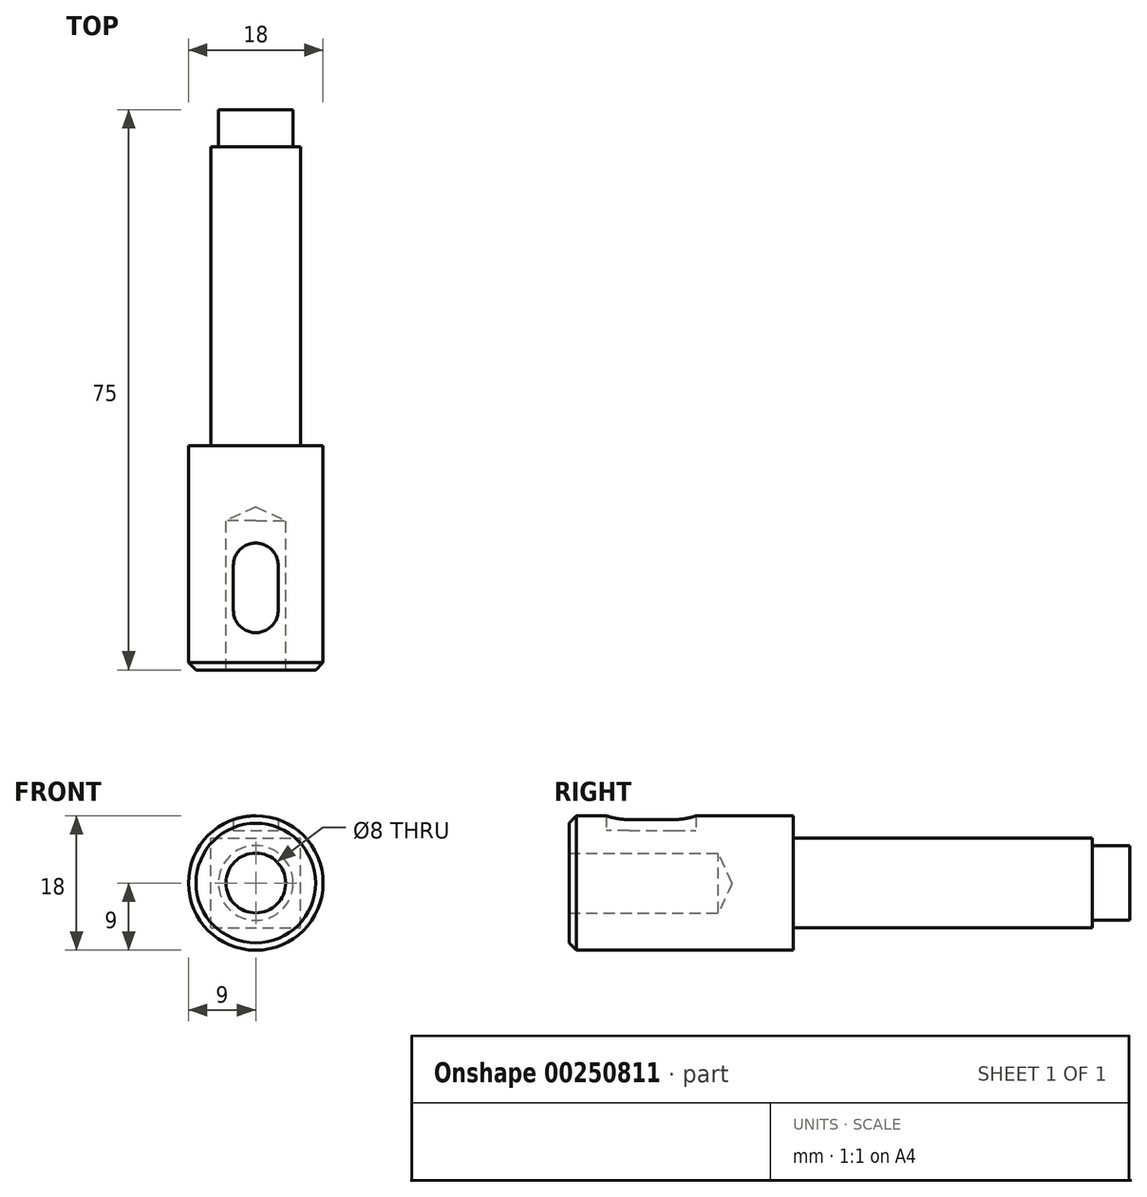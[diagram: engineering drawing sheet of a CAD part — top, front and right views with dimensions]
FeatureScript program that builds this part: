
annotation { "Feature Type Name" : "Feature", "Feature Type Description" : "" }
export const myFeature = defineFeature(function(context is Context, id is Id, definition is map)
    precondition{}
    {
        {
            var Q0;
            Q0=qCreatedBy(makeId("Top.planeOp"),FACE);
            var sketch = newSketch(context, id + "F0", { "sketchPlane" : qUnion([Q0])});
            skLineSegment(sketch, "E0", {"start": v(0, 53.17) * mm, "end": v(5, 53.17) * mm});
            skLineSegment(sketch, "E1", {"start": v(5, 53.17) * mm, "end": v(5, 48.17) * mm});
            skLineSegment(sketch, "E2", {"start": v(5, 48.17) * mm, "end": v(6, 48.17) * mm});
            skLineSegment(sketch, "E3", {"start": v(6, 48.17) * mm, "end": v(6, 8.17) * mm});
            skLineSegment(sketch, "E4", {"start": v(6, 8.17) * mm, "end": v(9, 8.17) * mm});
            skLineSegment(sketch, "E5", {"start": v(9, 8.17) * mm, "end": v(9, -20.83) * mm});
            skLineSegment(sketch, "E6", {"start": v(9, -20.83) * mm, "end": v(8, -21.83) * mm});
            skLineSegment(sketch, "E7", {"start": v(8, -21.83) * mm, "end": v(4, -21.83) * mm});
            skLineSegment(sketch, "E8", {"start": v(4, -21.83) * mm, "end": v(4, -6.83) * mm});
            skLineSegment(sketch, "E9", {"start": v(4, -6.83) * mm, "end": v(4, -1.83) * mm});
            skLineSegment(sketch, "E10", {"start": v(4, -1.83) * mm, "end": v(0, 0) * mm});
            skLineSegment(sketch, "E11", {"start": v(0, 53.17) * mm, "end": v(0, 0) * mm});
            skSolve(sketch);
        }
        {
            var Q0;
            Q0=makeQuery(id+"F0.imprint","IMPRINT",FACE,{"disambiguationData":[TD([[makeQuery(id+"F0.imprint","IMPRINT",EDGE,{"derivedFrom":sQuery(id+"F0.wireOp",EDGE,"E0")}),-1.0]])]});
            var Q1;
            Q1=sQuery(id+"F0.wireOp",EDGE,"E11");
            revolve(context, id + "F1", {"surfaceOperationType" : NewSurfaceOperationType.NEW, "entities" : qUnion([Q0]), "axis" : qUnion([Q1]), "revolveType" : RevolveType.FULL});
        }
        {
            var Q0;
            Q0=qCreatedBy(makeId("Top.planeOp"),FACE);
            cPlane(context, id + "F2", {"entities" : qUnion([Q0]), "cplaneType" : CPlaneType.OFFSET, "offset" : 7 * mm, "width" : 150 * mm, "height" : 150 * mm});
        }
        {
            var Q0;
            Q0=qCreatedBy(id+"F2.planeOp",FACE);
            var sketch = newSketch(context, id + "F3", { "sketchPlane" : qUnion([Q0])});
            skLineSegment(sketch, "E12", {"start": v(0, -13.83) * mm, "end": v(0, -7.83) * mm});
            skArc(sketch, "E13.0.startCap", {"start": v(3, -13.83) * mm, "mid": v(0, -16.83) * mm, "end": v(-3, -13.83) * mm});
            skArc(sketch, "E13.0.endCap", {"start": v(-3, -7.83) * mm, "mid": v(0, -4.83) * mm, "end": v(3, -7.83) * mm});
            skLineSegment(sketch, "E13.0.left", {"start": v(-3, -13.83) * mm, "end": v(-3, -7.83) * mm});
            skLineSegment(sketch, "E13.0.right", {"start": v(3, -13.83) * mm, "end": v(3, -7.83) * mm});
            skSolve(sketch);
        }
        {
            var Q0;
            Q0 = qSketchRegion(id + "F3", true);
            extrude(context, id + "F4", {"entities" : qUnion([Q0]), "operationType" : NewBodyOperationType.REMOVE, "depth" : 25 * mm, "offsetDistance" : 25 * mm});
        }
        {
            var Q0;
            Q0=makeQuery(id+"F1.opRevolve","SWEPT_FACE",FACE,{"disambiguationData":[OSD([sQuery(id+"F0.wireOp",EDGE,"E2")])]});
            var sketch = newSketch(context, id + "F5", { "sketchPlane" : qUnion([Q0])});
            skLineSegment(sketch, "E14.bottom", {"start": v(-6, 6) * mm, "end": v(6, 6) * mm});
            skLineSegment(sketch, "E14.top", {"start": v(-6, -6) * mm, "end": v(6, -6) * mm});
            skLineSegment(sketch, "E14.left", {"start": v(-6, 6) * mm, "end": v(-6, -6) * mm});
            skLineSegment(sketch, "E14.right", {"start": v(6, 6) * mm, "end": v(6, -6) * mm});
            skPoint(sketch, "E14.middle", {"position": v(0, 0) * mm});
            skSolve(sketch);
        }
        {
            var Q0;
            {var subQ0=sQuery(id+"F5.wireOp",EDGE,"E14.left");var subQ1=sQuery(id+"F5.wireOp",EDGE,"E14.bottom");var subQ2=makeQuery(id+"F5.imprint","INTERSECT",VERTEX,{"derivedFrom":[subQ1,subQ0]});Q0=makeQuery(id+"F5.imprint","IMPRINT",FACE,{"disambiguationData":[TD([[makeQuery(id+"F5.imprint","IMPRINT",EDGE,{"disambiguationData":[TD([[subQ2,-1.0]])],"derivedFrom":subQ1}),-1.0]])]});}
            var Q1;
            {var subQ0=sQuery(id+"F5.wireOp",EDGE,"E14.left");var subQ1=sQuery(id+"F5.wireOp",EDGE,"E14.top");var subQ2=makeQuery(id+"F5.imprint","INTERSECT",VERTEX,{"derivedFrom":[subQ1,subQ0]});Q1=makeQuery(id+"F5.imprint","IMPRINT",FACE,{"disambiguationData":[TD([[makeQuery(id+"F5.imprint","IMPRINT",EDGE,{"disambiguationData":[TD([[subQ2,-1.0]])],"derivedFrom":subQ1}),1.0]])]});}
            var Q2;
            {var subQ0=sQuery(id+"F5.wireOp",EDGE,"E14.right");var subQ1=sQuery(id+"F5.wireOp",EDGE,"E14.top");var subQ2=makeQuery(id+"F5.imprint","INTERSECT",VERTEX,{"derivedFrom":[subQ1,subQ0]});Q2=makeQuery(id+"F5.imprint","IMPRINT",FACE,{"disambiguationData":[TD([[makeQuery(id+"F5.imprint","IMPRINT",EDGE,{"disambiguationData":[TD([[subQ2,1.0]])],"derivedFrom":subQ1}),1.0]])]});}
            var Q3;
            {var subQ0=sQuery(id+"F5.wireOp",EDGE,"E14.right");var subQ1=sQuery(id+"F5.wireOp",EDGE,"E14.bottom");var subQ2=makeQuery(id+"F5.imprint","INTERSECT",VERTEX,{"derivedFrom":[subQ1,subQ0]});Q3=makeQuery(id+"F5.imprint","IMPRINT",FACE,{"disambiguationData":[TD([[makeQuery(id+"F5.imprint","IMPRINT",EDGE,{"disambiguationData":[TD([[subQ2,1.0]])],"derivedFrom":subQ1}),-1.0]])]});}
            extrude(context, id + "F6", {"entities" : qUnion([Q0, Q1, Q2, Q3]), "operationType" : NewBodyOperationType.ADD, "endBound" : BoundingType.UP_TO_NEXT, "oppositeDirection" : true, "depth" : 25 * mm, "offsetDistance" : 25 * mm});
        }
    });
